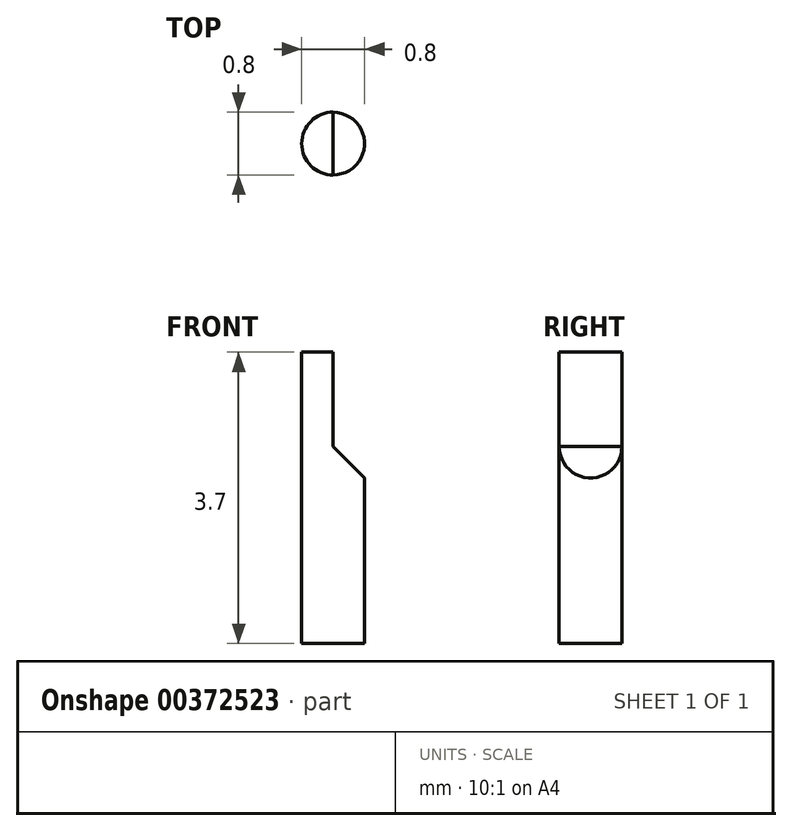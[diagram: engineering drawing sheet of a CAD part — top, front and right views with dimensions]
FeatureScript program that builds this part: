
annotation { "Feature Type Name" : "Feature", "Feature Type Description" : "" }
export const myFeature = defineFeature(function(context is Context, id is Id, definition is map)
    precondition{}
    {
        {
            var Q0;
            Q0=qCreatedBy(makeId("Top.planeOp"),FACE);
            var sketch = newSketch(context, id + "F0", { "sketchPlane" : qUnion([Q0])});
            skCircle(sketch, "E0", {"center": v(0, 0) * mm, "radius": 0.4 * mm});
            skSolve(sketch);
        }
        {
            var Q0;
            Q0=makeQuery(id+"F0.imprint","IMPRINT",FACE,{"disambiguationData":[TD([[makeQuery(id+"F0.imprint","IMPRINT",EDGE,{"derivedFrom":sQuery(id+"F0.wireOp",EDGE,"E0")}),1.0]])]});
            extrude(context, id + "F1", {"entities" : qUnion([Q0]), "depth" : 3.7 * mm});
        }
        {
            var Q0;
            Q0=makeQuery(id+"F1.opExtrude","SWEPT_BODY",BODY,{"disambiguationData":[OSD([sQuery(id+"F0.wireOp",EDGE,"E0")])]});
            transform(context, id + "F2", {"entities" : qUnion([Q0]), "transformType" : TransformType.TRANSLATION_3D, "dx" : 0 * mm, "dy" : 0 * mm, "dz" : 0 * mm, "makeCopy" : true});
        }
        {
            var Q0;
            Q0=qCreatedBy(makeId("Front.planeOp"),FACE);
            var sketch = newSketch(context, id + "F3", { "sketchPlane" : qUnion([Q0])});
            skLineSegment(sketch, "E1", {"start": v(0, 0) * mm, "end": v(0, 3.7) * mm, "construction": true});
            skLineSegment(sketch, "E2", {"start": v(0, 3.7) * mm, "end": v(0, 2.5) * mm});
            skLineSegment(sketch, "E3", {"start": v(0, 2.5) * mm, "end": v(0.4, 2.1) * mm});
            skLineSegment(sketch, "E4", {"start": v(0.4, 2.1) * mm, "end": v(0.4, 3.7) * mm});
            skLineSegment(sketch, "E5", {"start": v(0.4, 3.7) * mm, "end": v(0, 3.7) * mm});
            skSolve(sketch);
        }
        {
            var Q0;
            Q0=makeQuery(id+"F3.imprint","IMPRINT",FACE,{"disambiguationData":[TD([[makeQuery(id+"F3.imprint","IMPRINT",EDGE,{"derivedFrom":sQuery(id+"F3.wireOp",EDGE,"E2")}),1.0]])]});
            extrude(context, id + "F4", {"entities" : qUnion([Q0]), "operationType" : NewBodyOperationType.REMOVE, "endBound" : BoundingType.SYMMETRIC, "oppositeDirection" : true, "depth" : 1 * mm});
        }
    });
